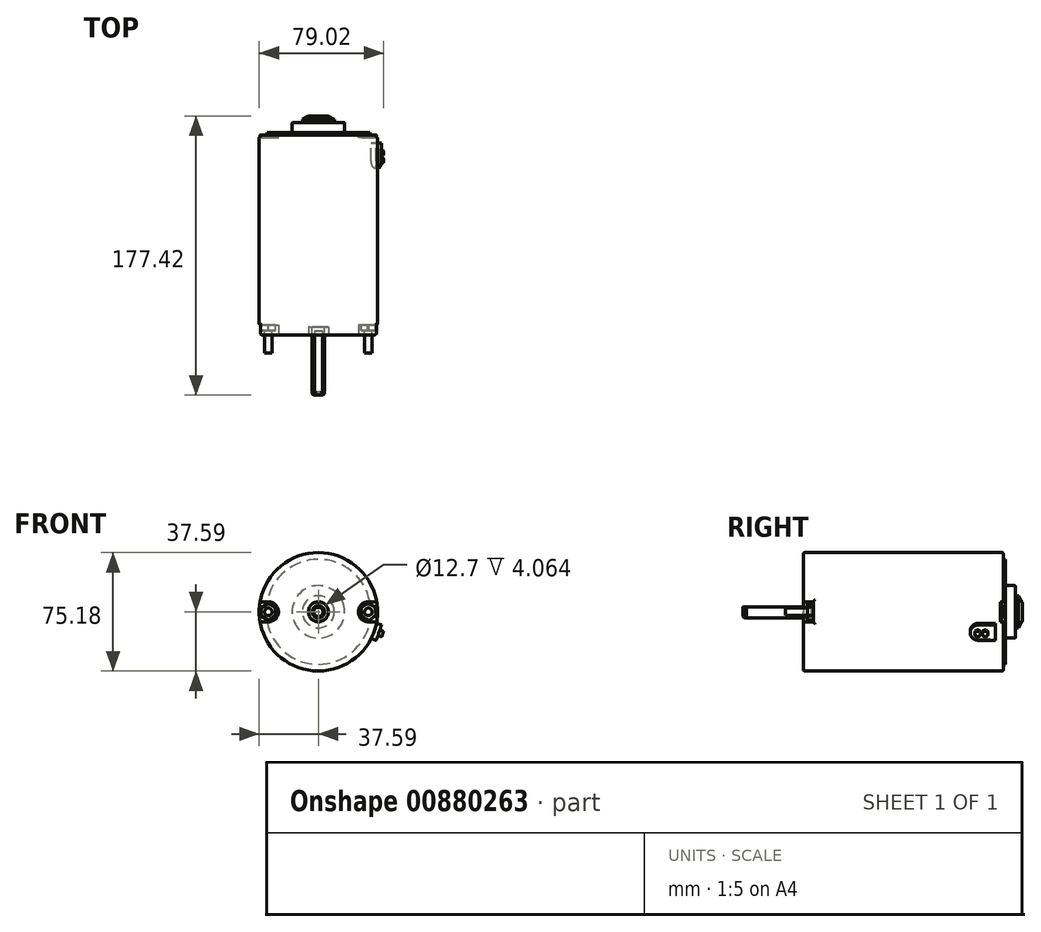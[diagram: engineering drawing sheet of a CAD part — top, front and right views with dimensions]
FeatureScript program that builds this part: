
annotation { "Feature Type Name" : "Feature", "Feature Type Description" : "" }
export const myFeature = defineFeature(function(context is Context, id is Id, definition is map)
    precondition{}
    {
        {
            var Q0;
            Q0=qCreatedBy(makeId("Front.planeOp"),FACE);
            var sketch = newSketch(context, id + "F0", { "sketchPlane" : qUnion([Q0])});
            skCircle(sketch, "E0", {"center": v(0, 0) * mm, "radius": 37.6 * mm});
            skSolve(sketch);
        }
        {
            var Q0;
            Q0=qSketchRegion(id+"F0",true);
            extrude(context, id + "F1", {"entities" : qUnion([Q0]), "depth" : 127 * mm});
        }
        {
            var Q0;
            Q0=makeQuery(id+"F1.opExtrude","CAP_FACE",FACE,{"disambiguationData":[OSD([sQuery(id+"F0.wireOp",EDGE,"E0")])],"isStart":false});
            var sketch = newSketch(context, id + "F2", { "sketchPlane" : qUnion([Q0])});
            skCircle(sketch, "E1", {"center": v(0, 0) * mm, "radius": 6.35 * mm});
            skSolve(sketch);
        }
        {
            var Q0;
            Q0=qSketchRegion(id+"F2",true);
            extrude(context, id + "F3", {"entities" : qUnion([Q0]), "operationType" : NewBodyOperationType.REMOVE, "oppositeDirection" : true, "depth" : 5.08 * mm});
        }
        {
            var Q0;
            Q0=makeQuery(id+"F3.boolean.opBoolean","COPY",FACE,{"derivedFrom":makeQuery(id+"F3.opExtrude","CAP_FACE",FACE,{"disambiguationData":[OSD([sQuery(id+"F2.wireOp",EDGE,"E1")])],"isStart":false})});
            var sketch = newSketch(context, id + "F4", { "sketchPlane" : qUnion([Q0])});
            skCircle(sketch, "E2", {"center": v(0, 0) * mm, "radius": 3.96 * mm});
            skSolve(sketch);
        }
        {
            var Q0;
            Q0=qSketchRegion(id+"F4",true);
            extrude(context, id + "F5", {"entities" : qUnion([Q0]), "operationType" : NewBodyOperationType.ADD, "depth" : 43.43 * mm});
        }
        {
            var Q0;
            Q0=makeQuery(id+"F5.opExtrude","CAP_EDGE",EDGE,{"disambiguationData":[OSD([sQuery(id+"F4.wireOp",EDGE,"E2")])],"isStart":false});
            chamfer(context, id + "F6", {"entities" : qUnion([Q0]), "width" : 1.02 * mm, "tangentPropagation" : true});
        }
        {
            var Q0;
            Q0=makeQuery(id+"F5.opExtrude","CAP_FACE",FACE,{"disambiguationData":[OSD([sQuery(id+"F4.wireOp",EDGE,"E2")])],"isStart":false});
            var sketch = newSketch(context, id + "F7", { "sketchPlane" : qUnion([Q0])});
            skLineSegment(sketch, "E3", {"start": v(-2.56, 3.02) * mm, "end": v(2.56, 3.02) * mm});
            skArc(sketch, "E4.0", {"start": v(2.56, 3.02) * mm, "mid": v(0, 3.96) * mm, "end": v(-2.56, 3.02) * mm});
            skLineSegment(sketch, "E5", {"start": v(0, 3.02) * mm, "end": v(0, -3.96) * mm, "construction": true});
            skPoint(sketch, "E6.orphan", {"position": v(-4.9, 3.02) * mm});
            skPoint(sketch, "E7.orphan", {"position": v(4.9, 3.02) * mm});
            skSolve(sketch);
        }
        {
            var Q0;
            Q0=qSketchRegion(id+"F7",true);
            var Q1;
            Q1=makeQuery(id+"F3.boolean.opBoolean","COPY",FACE,{"derivedFrom":makeQuery(id+"F3.opExtrude","CAP_FACE",FACE,{"disambiguationData":[OSD([sQuery(id+"F2.wireOp",EDGE,"E1")])],"isStart":false})});
            extrude(context, id + "F8", {"entities" : qUnion([Q0]), "operationType" : NewBodyOperationType.REMOVE, "oppositeDirection" : true, "endBoundEntityFace" : qUnion([Q1]), "depth" : 40.64 * mm});
        }
        {
            var Q0;
            Q0=makeQuery(id+"F5.opExtrude","CAP_FACE",FACE,{"disambiguationData":[OSD([sQuery(id+"F4.wireOp",EDGE,"E2")])],"isStart":false});
            cPlane(context, id + "F9", {"entities" : qUnion([Q0]), "cplaneType" : CPlaneType.OFFSET, "offset" : 1.6 * mm, "oppositeDirection" : true, "width" : 152.4 * mm, "height" : 152.4 * mm});
        }
        {
            var Q0;
            Q0=qCreatedBy(id+"F9.planeOp",FACE);
            var sketch = newSketch(context, id + "F10", { "sketchPlane" : qUnion([Q0])});
            skCircle(sketch, "E8", {"center": v(0, 0) * mm, "radius": 3.58 * mm});
            skCircle(sketch, "E9", {"center": v(0, 0) * mm, "radius": 4.9 * mm});
            skSolve(sketch);
        }
        {
            var Q0;
            Q0=qSketchRegion(id+"F10",true);
            extrude(context, id + "F11", {"entities" : qUnion([Q0]), "operationType" : NewBodyOperationType.REMOVE, "oppositeDirection" : true, "depth" : 0.79 * mm});
        }
        {
            var Q0;
            Q0=makeQuery(id+"F1.opExtrude","CAP_FACE",FACE,{"disambiguationData":[OSD([sQuery(id+"F0.wireOp",EDGE,"E0")])],"isStart":false});
            var sketch = newSketch(context, id + "F12", { "sketchPlane" : qUnion([Q0])});
            skArc(sketch, "E10", {"start": v(31.75, 6.35) * mm, "mid": v(25.4, 0) * mm, "end": v(31.75, -6.35) * mm});
            skArc(sketch, "E11", {"start": v(-31.75, -6.35) * mm, "mid": v(-25.4, 0) * mm, "end": v(-31.75, 6.35) * mm});
            skLineSegment(sketch, "E12", {"start": v(-31.75, 0) * mm, "end": v(31.75, 0) * mm, "construction": true});
            skLineSegment(sketch, "E13", {"start": v(-31.75, -6.35) * mm, "end": v(-52.48, -6.35) * mm});
            skLineSegment(sketch, "E14", {"start": v(-52.48, -6.35) * mm, "end": v(-52.48, 6.35) * mm});
            skLineSegment(sketch, "E15", {"start": v(-52.48, 6.35) * mm, "end": v(-31.75, 6.35) * mm});
            skLineSegment(sketch, "E16", {"start": v(31.75, -6.35) * mm, "end": v(43.63, -6.35) * mm});
            skLineSegment(sketch, "E17", {"start": v(43.63, -6.35) * mm, "end": v(43.63, 6.35) * mm});
            skLineSegment(sketch, "E18", {"start": v(43.63, 6.35) * mm, "end": v(31.75, 6.35) * mm});
            skSolve(sketch);
        }
        {
            var Q0;
            Q0=qSketchRegion(id+"F12",true);
            extrude(context, id + "F13", {"entities" : qUnion([Q0]), "operationType" : NewBodyOperationType.REMOVE, "oppositeDirection" : true, "depth" : 6.35 * mm});
        }
        {
            var Q0;
            Q0=makeQuery(id+"F1.opExtrude","CAP_FACE",FACE,{"disambiguationData":[OSD([sQuery(id+"F0.wireOp",EDGE,"E0")])],"isStart":false});
            fillet(context, id + "F14", {"entities" : qUnion([Q0]), "radius" : 1.02 * mm, "tangentPropagation" : true, "allowEdgeOverflow" : false});
        }
        {
            var Q0;
            Q0=makeQuery(id+"F13.boolean.opBoolean","INTERSECT",EDGE,{"derivedFrom":[makeQuery(id+"F1.opExtrude","SWEPT_FACE",FACE,{"disambiguationData":[OSD([sQuery(id+"F0.wireOp",EDGE,"E0")])]}),makeQuery(id+"F13.opExtrude","CAP_FACE",FACE,{"disambiguationData":[OSD([sQuery(id+"F12.wireOp",EDGE,"E11"),sQuery(id+"F12.wireOp",EDGE,"E13"),sQuery(id+"F12.wireOp",EDGE,"E14"),sQuery(id+"F12.wireOp",EDGE,"E15")])],"isStart":false})]});
            var Q1;
            Q1=makeQuery(id+"F13.boolean.opBoolean","INTERSECT",EDGE,{"derivedFrom":[makeQuery(id+"F1.opExtrude","SWEPT_FACE",FACE,{"disambiguationData":[OSD([sQuery(id+"F0.wireOp",EDGE,"E0")])]}),makeQuery(id+"F13.opExtrude","SWEPT_FACE",FACE,{"disambiguationData":[OSD([sQuery(id+"F12.wireOp",EDGE,"E15")])]})]});
            var Q2;
            Q2=makeQuery(id+"F13.boolean.opBoolean","INTERSECT",EDGE,{"derivedFrom":[makeQuery(id+"F1.opExtrude","SWEPT_FACE",FACE,{"disambiguationData":[OSD([sQuery(id+"F0.wireOp",EDGE,"E0")])]}),makeQuery(id+"F13.opExtrude","SWEPT_FACE",FACE,{"disambiguationData":[OSD([sQuery(id+"F12.wireOp",EDGE,"E13")])]})]});
            var Q3;
            Q3=makeQuery(id+"F13.boolean.opBoolean","INTERSECT",EDGE,{"derivedFrom":[makeQuery(id+"F1.opExtrude","SWEPT_FACE",FACE,{"disambiguationData":[OSD([sQuery(id+"F0.wireOp",EDGE,"E0")])]}),makeQuery(id+"F13.opExtrude","SWEPT_FACE",FACE,{"disambiguationData":[OSD([sQuery(id+"F12.wireOp",EDGE,"E16")])]})]});
            var Q4;
            Q4=makeQuery(id+"F13.boolean.opBoolean","INTERSECT",EDGE,{"derivedFrom":[makeQuery(id+"F1.opExtrude","SWEPT_FACE",FACE,{"disambiguationData":[OSD([sQuery(id+"F0.wireOp",EDGE,"E0")])]}),makeQuery(id+"F13.opExtrude","CAP_FACE",FACE,{"disambiguationData":[OSD([sQuery(id+"F12.wireOp",EDGE,"E10"),sQuery(id+"F12.wireOp",EDGE,"E16"),sQuery(id+"F12.wireOp",EDGE,"E17"),sQuery(id+"F12.wireOp",EDGE,"E18")])],"isStart":false})]});
            var Q5;
            Q5=makeQuery(id+"F13.boolean.opBoolean","INTERSECT",EDGE,{"derivedFrom":[makeQuery(id+"F1.opExtrude","SWEPT_FACE",FACE,{"disambiguationData":[OSD([sQuery(id+"F0.wireOp",EDGE,"E0")])]}),makeQuery(id+"F13.opExtrude","SWEPT_FACE",FACE,{"disambiguationData":[OSD([sQuery(id+"F12.wireOp",EDGE,"E18")])]})]});
            fillet(context, id + "F15", {"entities" : qUnion([Q0, Q1, Q2, Q3, Q4, Q5]), "radius" : 1.02 * mm, "tangentPropagation" : true, "allowEdgeOverflow" : false});
        }
        {
            var Q0;
            Q0=makeQuery(id+"F13.boolean.opBoolean","COPY",FACE,{"derivedFrom":makeQuery(id+"F13.opExtrude","CAP_FACE",FACE,{"disambiguationData":[OSD([sQuery(id+"F12.wireOp",EDGE,"E11"),sQuery(id+"F12.wireOp",EDGE,"E13"),sQuery(id+"F12.wireOp",EDGE,"E14"),sQuery(id+"F12.wireOp",EDGE,"E15")])],"isStart":false})});
            var sketch = newSketch(context, id + "F16", { "sketchPlane" : qUnion([Q0])});
            skCircle(sketch, "E19", {"center": v(-31.75, 0) * mm, "radius": 2.37 * mm});
            skCircle(sketch, "E20", {"center": v(31.75, 0) * mm, "radius": 2.37 * mm});
            skSolve(sketch);
        }
        {
            var Q0;
            Q0=qSketchRegion(id+"F16",true);
            extrude(context, id + "F17", {"entities" : qUnion([Q0]), "operationType" : NewBodyOperationType.ADD, "depth" : 17.78 * mm});
        }
        {
            var Q0;
            Q0=makeQuery(id+"F13.boolean.opBoolean","COPY",FACE,{"derivedFrom":makeQuery(id+"F13.opExtrude","CAP_FACE",FACE,{"disambiguationData":[OSD([sQuery(id+"F12.wireOp",EDGE,"E11"),sQuery(id+"F12.wireOp",EDGE,"E13"),sQuery(id+"F12.wireOp",EDGE,"E14"),sQuery(id+"F12.wireOp",EDGE,"E15")])],"isStart":false})});
            var sketch = newSketch(context, id + "F18", { "sketchPlane" : qUnion([Q0])});
            skCircle(sketch, "E21.cCircle", {"center": v(-31.75, 0) * mm, "radius": 5.33 * mm, "construction": true});
            skLineSegment(sketch, "E21.0", {"start": v(-36.4, 2.6) * mm, "end": v(-31.82, 5.33) * mm});
            skLineSegment(sketch, "E21.1", {"start": v(-31.82, 5.33) * mm, "end": v(-27.17, 2.73) * mm});
            skLineSegment(sketch, "E21.2", {"start": v(-27.17, 2.73) * mm, "end": v(-27.1, -2.6) * mm});
            skLineSegment(sketch, "E21.3", {"start": v(-27.1, -2.6) * mm, "end": v(-31.68, -5.33) * mm});
            skLineSegment(sketch, "E21.4", {"start": v(-31.68, -5.33) * mm, "end": v(-36.33, -2.73) * mm});
            skLineSegment(sketch, "E21.5", {"start": v(-36.33, -2.73) * mm, "end": v(-36.4, 2.6) * mm});
            skCircle(sketch, "E22.cCircle", {"center": v(31.75, 0) * mm, "radius": 5.33 * mm, "construction": true});
            skLineSegment(sketch, "E22.0", {"start": v(36.55, -2.33) * mm, "end": v(32.13, -5.32) * mm});
            skLineSegment(sketch, "E22.1", {"start": v(32.13, -5.32) * mm, "end": v(27.33, -2.99) * mm});
            skLineSegment(sketch, "E22.2", {"start": v(27.33, -2.99) * mm, "end": v(26.95, 2.33) * mm});
            skLineSegment(sketch, "E22.3", {"start": v(26.95, 2.33) * mm, "end": v(31.37, 5.32) * mm});
            skLineSegment(sketch, "E22.4", {"start": v(31.37, 5.32) * mm, "end": v(36.17, 2.99) * mm});
            skLineSegment(sketch, "E22.5", {"start": v(36.17, 2.99) * mm, "end": v(36.55, -2.33) * mm});
            skSolve(sketch);
        }
        {
            var Q0;
            Q0=qSketchRegion(id+"F18",true);
            extrude(context, id + "F19", {"entities" : qUnion([Q0]), "operationType" : NewBodyOperationType.ADD, "depth" : 3.68 * mm});
        }
        {
            var Q0;
            Q0=makeQuery(id+"F1.opExtrude","CAP_FACE",FACE,{"disambiguationData":[OSD([sQuery(id+"F0.wireOp",EDGE,"E0")])],"isStart":true});
            var sketch = newSketch(context, id + "F20", { "sketchPlane" : qUnion([Q0])});
            skCircle(sketch, "E23", {"center": v(0, 0) * mm, "radius": 33.34 * mm});
            skSolve(sketch);
        }
        {
            var Q0;
            Q0=qSketchRegion(id+"F20",true);
            extrude(context, id + "F21", {"entities" : qUnion([Q0]), "operationType" : NewBodyOperationType.ADD, "depth" : 1.52 * mm});
        }
        {
            var Q0;
            Q0=makeQuery(id+"F21.opExtrude","CAP_FACE",FACE,{"disambiguationData":[OSD([sQuery(id+"F20.wireOp",EDGE,"E23")])],"isStart":false});
            var sketch = newSketch(context, id + "F22", { "sketchPlane" : qUnion([Q0])});
            skCircle(sketch, "E24", {"center": v(0, 0) * mm, "radius": 16.64 * mm});
            skSolve(sketch);
        }
        {
            var Q0;
            Q0=qSketchRegion(id+"F22",true);
            extrude(context, id + "F23", {"entities" : qUnion([Q0]), "operationType" : NewBodyOperationType.ADD, "depth" : 6.35 * mm});
        }
        {
            var Q0;
            Q0=makeQuery(id+"F23.opExtrude","CAP_FACE",FACE,{"disambiguationData":[OSD([sQuery(id+"F22.wireOp",EDGE,"E24")])],"isStart":false});
            var sketch = newSketch(context, id + "F24", { "sketchPlane" : qUnion([Q0])});
            skCircle(sketch, "E25", {"center": v(0, 0) * mm, "radius": 10.16 * mm});
            skSolve(sketch);
        }
        {
            var Q0;
            Q0=qSketchRegion(id+"F24",true);
            extrude(context, id + "F25", {"entities" : qUnion([Q0]), "operationType" : NewBodyOperationType.ADD, "depth" : 4.2 * mm});
        }
        {
            var Q0;
            Q0=makeQuery(id+"F25.opExtrude","CAP_EDGE",EDGE,{"disambiguationData":[OSD([sQuery(id+"F24.wireOp",EDGE,"E25")])],"isStart":false});
            chamfer(context, id + "F26", {"entities" : qUnion([Q0]), "chamferType" : ChamferType.TWO_OFFSETS, "width1" : 2.3 * mm, "oppositeDirection" : false, "width2" : 4.2 * mm, "tangentPropagation" : true});
        }
        {
            var Q0;
            {var subQ0=sQuery(id+"F24.wireOp",EDGE,"E25");Q0=makeQuery(id+"F26.opChamfer","BLEND_EDGE",EDGE,{"blendedFrom":[makeQuery(id+"F25.opExtrude","CAP_EDGE",EDGE,{"disambiguationData":[OSD([subQ0])],"isStart":false}),makeQuery(id+"F25.opExtrude","CAP_FACE",FACE,{"disambiguationData":[OSD([subQ0])],"isStart":false})],"blendedInto":[makeQuery(id+"F25.opExtrude","CAP_FACE",FACE,{"disambiguationData":[OSD([subQ0])],"isStart":false})]});}
            var Q1;
            Q1=makeQuery(id+"F23.opExtrude","CAP_EDGE",EDGE,{"disambiguationData":[OSD([sQuery(id+"F22.wireOp",EDGE,"E24")])],"isStart":false});
            var Q2;
            Q2=makeQuery(id+"F1.opExtrude","CAP_EDGE",EDGE,{"disambiguationData":[OSD([sQuery(id+"F0.wireOp",EDGE,"E0")])],"isStart":true});
            fillet(context, id + "F27", {"entities" : qUnion([Q0, Q1, Q2]), "radius" : 0.5 * mm, "tangentPropagation" : true, "allowEdgeOverflow" : false});
        }
        {
            var Q0;
            Q0=makeQuery(id+"F21.opExtrude","CAP_FACE",FACE,{"disambiguationData":[OSD([sQuery(id+"F20.wireOp",EDGE,"E23")])],"isStart":false});
            var sketch = newSketch(context, id + "F28", { "sketchPlane" : qUnion([Q0])});
            skArc(sketch, "E26", {"start": v(-31.75, -6.35) * mm, "mid": v(-25.4, 0) * mm, "end": v(-31.75, 6.35) * mm});
            skArc(sketch, "E27", {"start": v(31.75, 6.35) * mm, "mid": v(25.4, 0) * mm, "end": v(31.75, -6.35) * mm});
            skLineSegment(sketch, "E28", {"start": v(-31.75, 0) * mm, "end": v(31.75, 0) * mm});
            skLineSegment(sketch, "E29", {"start": v(-31.75, -6.35) * mm, "end": v(-50.26, -6.35) * mm});
            skLineSegment(sketch, "E30", {"start": v(-50.26, -6.35) * mm, "end": v(-50.26, 6.35) * mm});
            skLineSegment(sketch, "E31", {"start": v(-50.26, 6.35) * mm, "end": v(-31.75, 6.35) * mm});
            skLineSegment(sketch, "E32", {"start": v(31.75, 6.35) * mm, "end": v(48.33, 6.35) * mm});
            skLineSegment(sketch, "E33", {"start": v(48.33, 6.35) * mm, "end": v(48.33, -6.35) * mm});
            skLineSegment(sketch, "E34", {"start": v(48.33, -6.35) * mm, "end": v(31.75, -6.35) * mm});
            skSolve(sketch);
        }
        {
            var Q0;
            Q0=qSketchRegion(id+"F28",true);
            extrude(context, id + "F29", {"entities" : qUnion([Q0]), "operationType" : NewBodyOperationType.REMOVE, "oppositeDirection" : true, "depth" : 3.17 * mm});
        }
        {
            var Q0;
            Q0=makeQuery(id+"F29.boolean.opBoolean","COPY",FACE,{"derivedFrom":makeQuery(id+"F29.opExtrude","CAP_FACE",FACE,{"disambiguationData":[OSD([sQuery(id+"F28.wireOp",EDGE,"E27"),sQuery(id+"F28.wireOp",EDGE,"E32"),sQuery(id+"F28.wireOp",EDGE,"E33"),sQuery(id+"F28.wireOp",EDGE,"E34")])],"isStart":false})});
            var sketch = newSketch(context, id + "F30", { "sketchPlane" : qUnion([Q0])});
            skCircle(sketch, "E35", {"center": v(31.75, 0) * mm, "radius": 4.25 * mm});
            skCircle(sketch, "E36", {"center": v(-31.75, 0) * mm, "radius": 4.25 * mm});
            skSolve(sketch);
        }
        {
            var Q0;
            Q0=qSketchRegion(id+"F30",true);
            extrude(context, id + "F31", {"entities" : qUnion([Q0]), "operationType" : NewBodyOperationType.ADD, "depth" : 1.4 * mm});
        }
        {
            var Q0;
            Q0=makeQuery(id+"F29.boolean.opBoolean","COPY",FACE,{"derivedFrom":makeQuery(id+"F29.opExtrude","CAP_FACE",FACE,{"disambiguationData":[OSD([sQuery(id+"F28.wireOp",EDGE,"E26"),sQuery(id+"F28.wireOp",EDGE,"E29"),sQuery(id+"F28.wireOp",EDGE,"E30"),sQuery(id+"F28.wireOp",EDGE,"E31")])],"isStart":false})});
            var sketch = newSketch(context, id + "F32", { "sketchPlane" : qUnion([Q0])});
            skLineSegment(sketch, "E37", {"start": v(0, 0) * mm, "end": v(-38.43, -13.23) * mm});
            skLineSegment(sketch, "E38", {"start": v(0, 0) * mm, "end": v(-49.41, 0) * mm, "construction": true});
            skLineSegment(sketch, "E39", {"start": v(-40.08, -8.43) * mm, "end": v(-36.77, -18.03) * mm});
            skLineSegment(sketch, "E40", {"start": v(-40.08, -8.43) * mm, "end": v(-33.03, -6) * mm});
            skLineSegment(sketch, "E41", {"start": v(-33.03, -6) * mm, "end": v(-29.72, -15.6) * mm});
            skLineSegment(sketch, "E42", {"start": v(-29.72, -15.6) * mm, "end": v(-36.77, -18.03) * mm});
            skSolve(sketch);
        }
        {
            var Q0;
            Q0=qSketchRegion(id+"F32",true);
            extrude(context, id + "F33", {"entities" : qUnion([Q0]), "operationType" : NewBodyOperationType.ADD, "oppositeDirection" : true, "depth" : 19.3 * mm});
        }
        {
            var Q0;
            Q0=makeQuery(id+"F33.opExtrude","SWEPT_FACE",FACE,{"disambiguationData":[OSD([sQuery(id+"F32.wireOp",EDGE,"E39")])]});
            var sketch = newSketch(context, id + "F34", { "sketchPlane" : qUnion([Q0])});
            skArc(sketch, "E43", {"start": v(-15.87, 5.08) * mm, "mid": v(-20.96, 0) * mm, "end": v(-15.87, -5.08) * mm});
            skLineSegment(sketch, "E44.0", {"start": v(0, 5.9) * mm, "end": v(0, -37.08) * mm, "construction": true});
            skLineSegment(sketch, "E45.0", {"start": v(-15.87, -5.08) * mm, "end": v(-5.08, -5.08) * mm});
            skLineSegment(sketch, "E45.1", {"start": v(-20.96, 5.08) * mm, "end": v(-20.96, -5.08) * mm, "construction": true});
            skLineSegment(sketch, "E45.2", {"start": v(-15.87, 5.08) * mm, "end": v(-5.08, 5.08) * mm});
            skLineSegment(sketch, "E46", {"start": v(-5.08, -5.08) * mm, "end": v(-5.08, 5.08) * mm});
            skLineSegment(sketch, "E47.bottom", {"start": v(-26.14, -11.18) * mm, "end": v(4.57, -11.18) * mm});
            skLineSegment(sketch, "E47.top", {"start": v(-26.14, 9.91) * mm, "end": v(4.57, 9.91) * mm});
            skLineSegment(sketch, "E47.left", {"start": v(-26.14, -11.18) * mm, "end": v(-26.14, 9.91) * mm});
            skLineSegment(sketch, "E47.right", {"start": v(4.57, -11.18) * mm, "end": v(4.57, 9.91) * mm});
            skSolve(sketch);
        }
        {
            var Q0;
            {var subQ0=sQuery(id+"F34.wireOp",EDGE,"E43");var subQ1=sQuery(id+"F32.wireOp",EDGE,"E39");var subQ4=makeQuery(id+"F33.opExtrude","CAP_EDGE",EDGE,{"disambiguationData":[OSD([subQ1])],"isStart":false});var subQ5=makeQuery(id+"F34.imprint","INTERSECT",VERTEX,{"derivedFrom":[subQ4,subQ0]});Q0=makeQuery(id+"F34.imprint","IMPRINT",FACE,{"disambiguationData":[TD([[makeQuery(id+"F34.imprint","IMPRINT",EDGE,{"disambiguationData":[TD([[subQ5,-1.0]])],"derivedFrom":subQ4}),1.0]])]});}
            var Q1;
            {var subQ4=sQuery(id+"F34.wireOp",EDGE,"E45.0");Q1=makeQuery(id+"F34.imprint","IMPRINT",FACE,{"disambiguationData":[TD([[makeQuery(id+"F34.imprint","IMPRINT",EDGE,{"derivedFrom":subQ4}),-1.0]])]});}
            var Q2;
            {var subQ0=sQuery(id+"F34.wireOp",EDGE,"E43");var subQ1=sQuery(id+"F32.wireOp",EDGE,"E39");var subQ4=makeQuery(id+"F33.opExtrude","CAP_EDGE",EDGE,{"disambiguationData":[OSD([subQ1])],"isStart":false});var subQ5=makeQuery(id+"F34.imprint","INTERSECT",VERTEX,{"derivedFrom":[subQ4,subQ0]});Q2=makeQuery(id+"F34.imprint","IMPRINT",FACE,{"disambiguationData":[TD([[makeQuery(id+"F34.imprint","IMPRINT",EDGE,{"disambiguationData":[TD([[subQ5,1.0]])],"derivedFrom":subQ4}),1.0]])]});}
            var Q3;
            {var subQ0=sQuery(id+"F34.wireOp",EDGE,"E46");Q3=makeQuery(id+"F34.imprint","IMPRINT",FACE,{"disambiguationData":[TD([[makeQuery(id+"F34.imprint","IMPRINT",EDGE,{"derivedFrom":subQ0}),-1.0]])]});}
            var Q4;
            Q4=makeQuery(id+"F1.opExtrude","SWEPT_FACE",FACE,{"disambiguationData":[OSD([sQuery(id+"F0.wireOp",EDGE,"E0")])]});
            extrude(context, id + "F35", {"entities" : qUnion([Q0, Q1, Q2, Q3]), "operationType" : NewBodyOperationType.REMOVE, "endBound" : BoundingType.UP_TO_SURFACE, "oppositeDirection" : true, "endBoundEntityFace" : qUnion([Q4]), "depth" : 2.54 * mm});
        }
        {
            var Q0;
            Q0=makeQuery(id+"F33.opExtrude","SWEPT_FACE",FACE,{"disambiguationData":[OSD([sQuery(id+"F32.wireOp",EDGE,"E39")])]});
            var sketch = newSketch(context, id + "F36", { "sketchPlane" : qUnion([Q0])});
            skCircle(sketch, "E48", {"center": v(-16.18, 0) * mm, "radius": 1.84 * mm});
            skCircle(sketch, "E49", {"center": v(-11.43, 0) * mm, "radius": 1.84 * mm});
            skSolve(sketch);
        }
        {
            var Q0;
            Q0=qSketchRegion(id+"F36",true);
            extrude(context, id + "F37", {"entities" : qUnion([Q0]), "operationType" : NewBodyOperationType.ADD, "depth" : 2.54 * mm});
        }
    });
